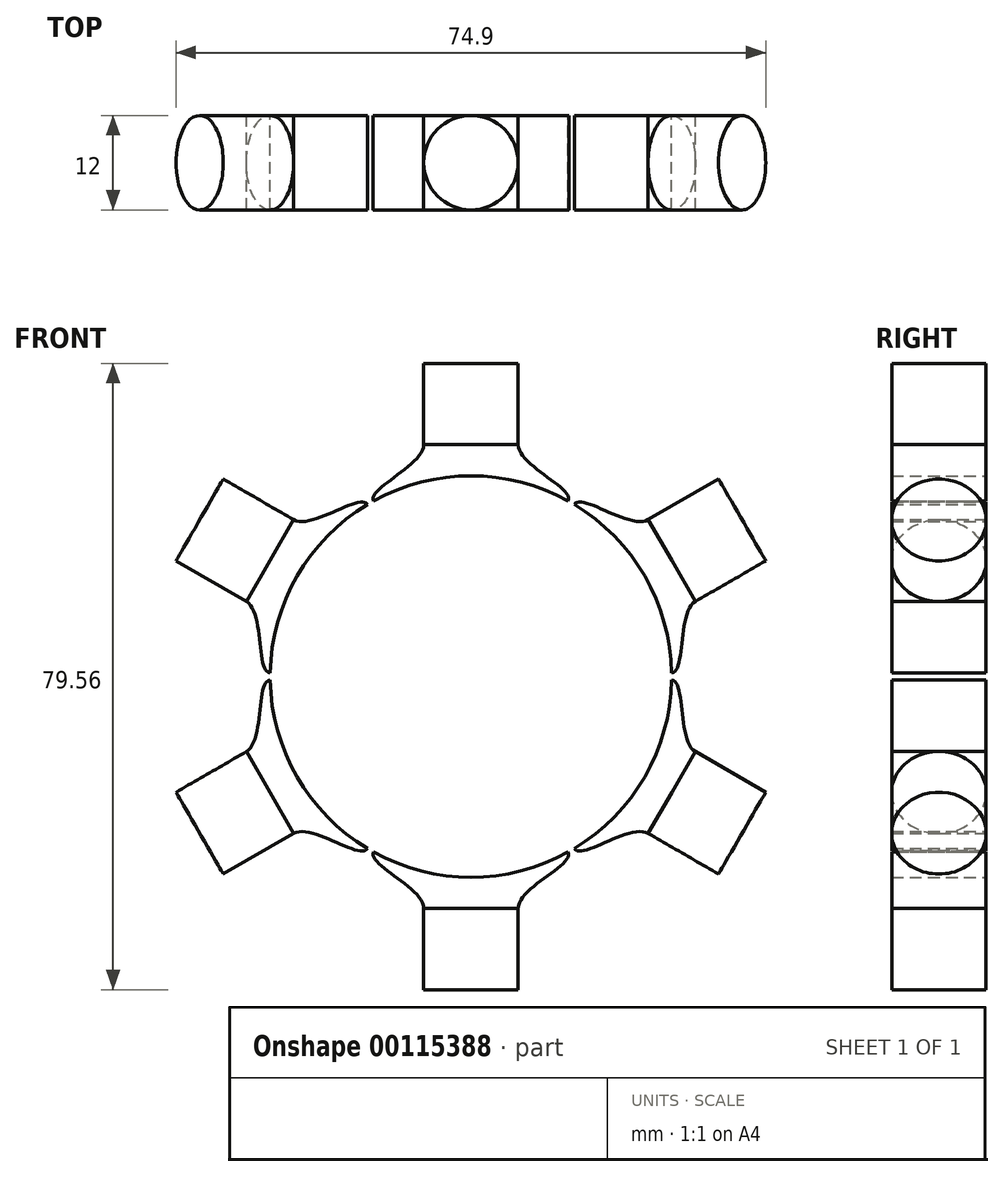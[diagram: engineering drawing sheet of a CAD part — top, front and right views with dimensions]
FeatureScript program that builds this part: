
annotation { "Feature Type Name" : "Feature", "Feature Type Description" : "" }
export const myFeature = defineFeature(function(context is Context, id is Id, definition is map)
    precondition{}
    {
        {
            var Q0;
            Q0=qCreatedBy(makeId("Front.planeOp"),FACE);
            var sketch = newSketch(context, id + "F0", { "sketchPlane" : qUnion([Q0])});
            skCircle(sketch, "E0", {"center": v(0, 0) * mm, "radius": 25.5 * mm});
            skLineSegment(sketch, "E1.top", {"start": v(-6, 39.78) * mm, "end": v(6, 39.78) * mm});
            skLineSegment(sketch, "E1.left", {"start": v(-6, 24.78) * mm, "end": v(-6, 39.78) * mm});
            skLineSegment(sketch, "E1.right", {"start": v(6, 24.78) * mm, "end": v(6, 39.78) * mm});
            skPoint(sketch, "E1.middle", {"position": v(0, 32.28) * mm});
            skFitSpline(sketch, "E2", {"points": [v(-12.35, 22.3) * mm, v(-6, 29.46) * mm], "startDerivative": vector(-2.75, 4.7) * mm, "endDerivative": vector(0, 8.03) * mm});
            skFitSpline(sketch, "E3.MirrorCS", {"points": [v(12.35, 22.3) * mm, v(6, 29.46) * mm], "startDerivative": vector(2.75, 4.7) * mm, "endDerivative": vector(0, 8.03) * mm});
            skLineSegment(sketch, "E4.1.0", {"start": v(-24.46, 7.2) * mm, "end": v(-37.45, 14.7) * mm});
            skLineSegment(sketch, "E4.1.1", {"start": v(-37.45, 14.7) * mm, "end": v(-31.45, 25.09) * mm});
            skLineSegment(sketch, "E4.1.2", {"start": v(-18.46, 17.59) * mm, "end": v(-31.45, 25.09) * mm});
            skLineSegment(sketch, "E4.2.0", {"start": v(-18.46, -17.59) * mm, "end": v(-31.45, -25.09) * mm});
            skLineSegment(sketch, "E4.2.1", {"start": v(-31.45, -25.09) * mm, "end": v(-37.45, -14.7) * mm});
            skLineSegment(sketch, "E4.2.2", {"start": v(-24.46, -7.2) * mm, "end": v(-37.45, -14.7) * mm});
            skLineSegment(sketch, "E4.3.0", {"start": v(6, -24.78) * mm, "end": v(6, -39.78) * mm});
            skLineSegment(sketch, "E4.3.1", {"start": v(6, -39.78) * mm, "end": v(-6, -39.78) * mm});
            skLineSegment(sketch, "E4.3.2", {"start": v(-6, -24.78) * mm, "end": v(-6, -39.78) * mm});
            skLineSegment(sketch, "E4.4.0", {"start": v(24.46, -7.2) * mm, "end": v(37.45, -14.7) * mm});
            skLineSegment(sketch, "E4.4.1", {"start": v(37.45, -14.7) * mm, "end": v(31.45, -25.09) * mm});
            skLineSegment(sketch, "E4.4.2", {"start": v(18.46, -17.59) * mm, "end": v(31.45, -25.09) * mm});
            skLineSegment(sketch, "E4.5.0", {"start": v(18.46, 17.59) * mm, "end": v(31.45, 25.09) * mm});
            skLineSegment(sketch, "E4.5.1", {"start": v(31.45, 25.09) * mm, "end": v(37.45, 14.7) * mm});
            skLineSegment(sketch, "E4.5.2", {"start": v(24.46, 7.2) * mm, "end": v(37.45, 14.7) * mm});
            skFitSpline(sketch, "E5.MirrorCS", {"points": [v(-12.35, -22.3) * mm, v(-6, -29.46) * mm], "startDerivative": vector(-2.75, -4.7) * mm, "endDerivative": vector(0, -8.03) * mm});
            skFitSpline(sketch, "E6.MirrorCS", {"points": [v(12.35, -22.3) * mm, v(6, -29.46) * mm], "startDerivative": vector(2.75, -4.7) * mm, "endDerivative": vector(0, -8.03) * mm});
            skFitSpline(sketch, "E7.MirrorCS", {"points": [v(13.14, 21.85) * mm, v(22.51, 19.93) * mm], "startDerivative": vector(2.7, 4.74) * mm, "endDerivative": vector(6.95, 4.01) * mm});
            skFitSpline(sketch, "E8.MirrorCS", {"points": [v(25.5, 0.46) * mm, v(28.51, 9.53) * mm], "startDerivative": vector(5.45, -0.03) * mm, "endDerivative": vector(6.95, 4.01) * mm});
            skFitSpline(sketch, "E9.MirrorCS", {"points": [v(25.5, -0.46) * mm, v(28.51, -9.53) * mm], "startDerivative": vector(5.45, 0.03) * mm, "endDerivative": vector(6.95, -4.01) * mm});
            skFitSpline(sketch, "E10.MirrorCS", {"points": [v(13.14, -21.85) * mm, v(22.51, -19.93) * mm], "startDerivative": vector(2.7, -4.74) * mm, "endDerivative": vector(6.95, -4.01) * mm});
            skFitSpline(sketch, "E11.MirrorCS", {"points": [v(-25.5, -0.46) * mm, v(-28.51, -9.53) * mm], "startDerivative": vector(-5.45, 0.03) * mm, "endDerivative": vector(-6.95, -4.01) * mm});
            skFitSpline(sketch, "E12.MirrorCS", {"points": [v(-13.14, -21.85) * mm, v(-22.51, -19.93) * mm], "startDerivative": vector(-2.7, -4.74) * mm, "endDerivative": vector(-6.95, -4.01) * mm});
            skFitSpline(sketch, "E13.MirrorCS", {"points": [v(-25.5, 0.46) * mm, v(-28.51, 9.53) * mm], "startDerivative": vector(-5.45, -0.03) * mm, "endDerivative": vector(-6.95, 4.01) * mm});
            skFitSpline(sketch, "E14.MirrorCS", {"points": [v(-13.14, 21.85) * mm, v(-22.51, 19.93) * mm], "startDerivative": vector(-2.7, 4.74) * mm, "endDerivative": vector(-6.95, 4.01) * mm});
            skCircle(sketch, "E15", {"center": v(0, 0) * mm, "radius": 38.5 * mm});
            skCircle(sketch, "E16.0", {"center": v(0, 0) * mm, "radius": 43.5 * mm});
            skLineSegment(sketch, "E17", {"start": v(-6, 29.46) * mm, "end": v(6, 29.46) * mm});
            skLineSegment(sketch, "E18.1.0", {"start": v(-28.51, 9.53) * mm, "end": v(-22.51, 19.93) * mm});
            skLineSegment(sketch, "E18.2.0", {"start": v(-22.51, -19.93) * mm, "end": v(-28.51, -9.53) * mm});
            skLineSegment(sketch, "E19.1.3.0", {"start": v(6, -29.46) * mm, "end": v(-6, -29.46) * mm});
            skLineSegment(sketch, "E19.1.4.0", {"start": v(28.51, -9.53) * mm, "end": v(22.51, -19.93) * mm});
            skLineSegment(sketch, "E19.1.5.0", {"start": v(22.51, 19.93) * mm, "end": v(28.51, 9.53) * mm});
            skSolve(sketch);
        }
        {
            var Q0;
            {var subQ1=sQuery(id+"F0.wireOp",EDGE,"E0");var subQ4=sQuery(id+"F0.wireOp",EDGE,"E1.left");var subQ9=makeQuery(id+"F0.imprint","INTERSECT",VERTEX,{"derivedFrom":[subQ1,subQ4]});Q0=makeQuery(id+"F0.imprint","IMPRINT",FACE,{"disambiguationData":[TD([[makeQuery(id+"F0.imprint","IMPRINT",EDGE,{"disambiguationData":[TD([[subQ9,1.0]])],"derivedFrom":subQ1}),-1.0]])]});}
            var Q1;
            {var subQ3=sQuery(id+"F0.wireOp",EDGE,"E3.MirrorCS");Q1=makeQuery(id+"F0.imprint","IMPRINT",FACE,{"disambiguationData":[TD([[makeQuery(id+"F0.imprint","IMPRINT",EDGE,{"derivedFrom":subQ3}),1.0]])]});}
            var Q2;
            {var subQ3=sQuery(id+"F0.wireOp",EDGE,"E2");Q2=makeQuery(id+"F0.imprint","IMPRINT",FACE,{"disambiguationData":[TD([[makeQuery(id+"F0.imprint","IMPRINT",EDGE,{"derivedFrom":subQ3}),-1.0]])]});}
            var Q3;
            {var subQ3=sQuery(id+"F0.wireOp",EDGE,"E14.MirrorCS");Q3=makeQuery(id+"F0.imprint","IMPRINT",FACE,{"disambiguationData":[TD([[makeQuery(id+"F0.imprint","IMPRINT",EDGE,{"derivedFrom":subQ3}),1.0]])]});}
            var Q4;
            {var subQ1=sQuery(id+"F0.wireOp",EDGE,"E0");var subQ6=sQuery(id+"F0.wireOp",EDGE,"E4.1.0");var subQ9=makeQuery(id+"F0.imprint","INTERSECT",VERTEX,{"derivedFrom":[subQ1,subQ6]});Q4=makeQuery(id+"F0.imprint","IMPRINT",FACE,{"disambiguationData":[TD([[makeQuery(id+"F0.imprint","IMPRINT",EDGE,{"disambiguationData":[TD([[subQ9,1.0]])],"derivedFrom":subQ1}),-1.0]])]});}
            var Q5;
            {var subQ3=sQuery(id+"F0.wireOp",EDGE,"E7.MirrorCS");Q5=makeQuery(id+"F0.imprint","IMPRINT",FACE,{"disambiguationData":[TD([[makeQuery(id+"F0.imprint","IMPRINT",EDGE,{"derivedFrom":subQ3}),-1.0]])]});}
            var Q6;
            {var subQ1=sQuery(id+"F0.wireOp",EDGE,"E0");var subQ4=sQuery(id+"F0.wireOp",EDGE,"E4.5.0");var subQ8=makeQuery(id+"F0.imprint","INTERSECT",VERTEX,{"derivedFrom":[subQ1,subQ4]});Q6=makeQuery(id+"F0.imprint","IMPRINT",FACE,{"disambiguationData":[TD([[makeQuery(id+"F0.imprint","IMPRINT",EDGE,{"disambiguationData":[TD([[subQ8,1.0]])],"derivedFrom":subQ1}),-1.0]])]});}
            var Q7;
            {var subQ3=sQuery(id+"F0.wireOp",EDGE,"E8.MirrorCS");Q7=makeQuery(id+"F0.imprint","IMPRINT",FACE,{"disambiguationData":[TD([[makeQuery(id+"F0.imprint","IMPRINT",EDGE,{"derivedFrom":subQ3}),1.0]])]});}
            var Q8;
            {var subQ3=sQuery(id+"F0.wireOp",EDGE,"E13.MirrorCS");Q8=makeQuery(id+"F0.imprint","IMPRINT",FACE,{"disambiguationData":[TD([[makeQuery(id+"F0.imprint","IMPRINT",EDGE,{"derivedFrom":subQ3}),-1.0]])]});}
            var Q9;
            {var subQ3=sQuery(id+"F0.wireOp",EDGE,"E11.MirrorCS");Q9=makeQuery(id+"F0.imprint","IMPRINT",FACE,{"disambiguationData":[TD([[makeQuery(id+"F0.imprint","IMPRINT",EDGE,{"derivedFrom":subQ3}),1.0]])]});}
            var Q10;
            {var subQ0=sQuery(id+"F0.wireOp",EDGE,"E4.2.0");var subQ4=sQuery(id+"F0.wireOp",EDGE,"E0");var subQ5=makeQuery(id+"F0.imprint","INTERSECT",VERTEX,{"derivedFrom":[subQ4,subQ0]});Q10=makeQuery(id+"F0.imprint","IMPRINT",FACE,{"disambiguationData":[TD([[makeQuery(id+"F0.imprint","IMPRINT",EDGE,{"disambiguationData":[TD([[subQ5,1.0]])],"derivedFrom":subQ4}),-1.0]])]});}
            var Q11;
            {var subQ3=sQuery(id+"F0.wireOp",EDGE,"E12.MirrorCS");Q11=makeQuery(id+"F0.imprint","IMPRINT",FACE,{"disambiguationData":[TD([[makeQuery(id+"F0.imprint","IMPRINT",EDGE,{"derivedFrom":subQ3}),-1.0]])]});}
            var Q12;
            {var subQ3=sQuery(id+"F0.wireOp",EDGE,"E5.MirrorCS");Q12=makeQuery(id+"F0.imprint","IMPRINT",FACE,{"disambiguationData":[TD([[makeQuery(id+"F0.imprint","IMPRINT",EDGE,{"derivedFrom":subQ3}),1.0]])]});}
            var Q13;
            {var subQ1=sQuery(id+"F0.wireOp",EDGE,"E0");var subQ4=sQuery(id+"F0.wireOp",EDGE,"E4.3.0");var subQ5=makeQuery(id+"F0.imprint","INTERSECT",VERTEX,{"derivedFrom":[subQ1,subQ4]});Q13=makeQuery(id+"F0.imprint","IMPRINT",FACE,{"disambiguationData":[TD([[makeQuery(id+"F0.imprint","IMPRINT",EDGE,{"disambiguationData":[TD([[subQ5,1.0]])],"derivedFrom":subQ1}),-1.0]])]});}
            var Q14;
            {var subQ3=sQuery(id+"F0.wireOp",EDGE,"E6.MirrorCS");Q14=makeQuery(id+"F0.imprint","IMPRINT",FACE,{"disambiguationData":[TD([[makeQuery(id+"F0.imprint","IMPRINT",EDGE,{"derivedFrom":subQ3}),-1.0]])]});}
            var Q15;
            {var subQ3=sQuery(id+"F0.wireOp",EDGE,"E10.MirrorCS");Q15=makeQuery(id+"F0.imprint","IMPRINT",FACE,{"disambiguationData":[TD([[makeQuery(id+"F0.imprint","IMPRINT",EDGE,{"derivedFrom":subQ3}),1.0]])]});}
            var Q16;
            {var subQ1=sQuery(id+"F0.wireOp",EDGE,"E0");var subQ4=sQuery(id+"F0.wireOp",EDGE,"E4.4.0");var subQ8=makeQuery(id+"F0.imprint","INTERSECT",VERTEX,{"derivedFrom":[subQ1,subQ4]});Q16=makeQuery(id+"F0.imprint","IMPRINT",FACE,{"disambiguationData":[TD([[makeQuery(id+"F0.imprint","IMPRINT",EDGE,{"disambiguationData":[TD([[subQ8,1.0]])],"derivedFrom":subQ1}),-1.0]])]});}
            var Q17;
            {var subQ3=sQuery(id+"F0.wireOp",EDGE,"E9.MirrorCS");Q17=makeQuery(id+"F0.imprint","IMPRINT",FACE,{"disambiguationData":[TD([[makeQuery(id+"F0.imprint","IMPRINT",EDGE,{"derivedFrom":subQ3}),-1.0]])]});}
            extrude(context, id + "F1", {"entities" : qUnion([Q0, Q1, Q2, Q3, Q4, Q5, Q6, Q7, Q8, Q9, Q10, Q11, Q12, Q13, Q14, Q15, Q16, Q17]), "endBound" : BoundingType.SYMMETRIC, "depth" : 12 * mm});
        }
        {
            var Q0;
            Q0=makeQuery(id+"F1.opExtrude","SWEPT_FACE",FACE,{"disambiguationData":[OSD([sQuery(id+"F0.wireOp",EDGE,"E17")])]});
            var sketch = newSketch(context, id + "F2", { "sketchPlane" : qUnion([Q0])});
            skCircle(sketch, "E20", {"center": v(0, 0) * mm, "radius": 6 * mm});
            skSolve(sketch);
        }
        {
            var Q0;
            {var subQ0=sQuery(id+"F2.wireOp",EDGE,"E20");var subQ1=sQuery(id+"F0.wireOp",EDGE,"E17");var subQ2=makeQuery(id+"F2.imprint","INTERSECT",VERTEX,{"derivedFrom":[makeQuery(id+"F1.opExtrude","CAP_EDGE",EDGE,{"disambiguationData":[OSD([subQ1])],"isStart":true}),subQ0]});Q0=makeQuery(id+"F2.imprint","IMPRINT",FACE,{"disambiguationData":[TD([[makeQuery(id+"F2.imprint","IMPRINT",EDGE,{"disambiguationData":[TD([[subQ2,1.0]])],"derivedFrom":subQ0}),1.0]])]});}
            extrude(context, id + "F3", {"entities" : qUnion([Q0]), "operationType" : NewBodyOperationType.ADD, "depth" : 10.32 * mm});
        }
        {
            var Q0;
            Q0=makeQuery(id+"F1.opExtrude","SWEPT_BODY",BODY,{"disambiguationData":[OSD([sQuery(id+"F0.wireOp",EDGE,"E0"),sQuery(id+"F0.wireOp",EDGE,"E2"),sQuery(id+"F0.wireOp",EDGE,"E3.MirrorCS"),sQuery(id+"F0.wireOp",EDGE,"E17")])]});
            var Q1;
            Q1=qCreatedBy(makeId("Top.planeOp"),FACE);
            mirror(context, id + "F4", {"operationType" : NewBodyOperationType.ADD, "entities" : qUnion([Q0]), "mirrorPlane" : qUnion([Q1])});
        }
        {
            var Q0;
            Q0=makeQuery(id+"F1.opExtrude","SWEPT_FACE",FACE,{"disambiguationData":[OSD([sQuery(id+"F0.wireOp",EDGE,"E19.1.5.0")])]});
            var sketch = newSketch(context, id + "F5", { "sketchPlane" : qUnion([Q0])});
            skCircle(sketch, "E21", {"center": v(0, 0) * mm, "radius": 6 * mm});
            skSolve(sketch);
        }
        {
            var Q0;
            {var subQ0=sQuery(id+"F5.wireOp",EDGE,"E21");var subQ1=sQuery(id+"F0.wireOp",EDGE,"E19.1.5.0");var subQ3=makeQuery(id+"F5.imprint","INTERSECT",VERTEX,{"derivedFrom":[makeQuery(id+"F1.opExtrude","CAP_EDGE",EDGE,{"disambiguationData":[OSD([subQ1])],"isStart":true}),subQ0]});Q0=makeQuery(id+"F5.imprint","IMPRINT",FACE,{"disambiguationData":[TD([[makeQuery(id+"F5.imprint","IMPRINT",EDGE,{"disambiguationData":[TD([[subQ3,-1.0]])],"derivedFrom":subQ0}),1.0]])]});}
            extrude(context, id + "F6", {"entities" : qUnion([Q0]), "operationType" : NewBodyOperationType.ADD, "depth" : 10.32 * mm});
        }
        {
            var Q0;
            Q0=makeQuery(id+"F1.opExtrude","SWEPT_FACE",FACE,{"disambiguationData":[OSD([sQuery(id+"F0.wireOp",EDGE,"E19.1.4.0")])]});
            var sketch = newSketch(context, id + "F7", { "sketchPlane" : qUnion([Q0])});
            skCircle(sketch, "E22", {"center": v(0, 0) * mm, "radius": 6 * mm});
            skSolve(sketch);
        }
        {
            var Q0;
            {var subQ0=sQuery(id+"F7.wireOp",EDGE,"E22");var subQ1=sQuery(id+"F0.wireOp",EDGE,"E19.1.4.0");var subQ3=makeQuery(id+"F7.imprint","INTERSECT",VERTEX,{"derivedFrom":[makeQuery(id+"F1.opExtrude","CAP_EDGE",EDGE,{"disambiguationData":[OSD([subQ1])],"isStart":true}),subQ0]});Q0=makeQuery(id+"F7.imprint","IMPRINT",FACE,{"disambiguationData":[TD([[makeQuery(id+"F7.imprint","IMPRINT",EDGE,{"disambiguationData":[TD([[subQ3,-1.0]])],"derivedFrom":subQ0}),1.0]])]});}
            extrude(context, id + "F8", {"entities" : qUnion([Q0]), "operationType" : NewBodyOperationType.ADD, "depth" : 10.32 * mm});
        }
        {
            var Q0;
            Q0=makeQuery(id+"F1.opExtrude","SWEPT_FACE",FACE,{"disambiguationData":[OSD([sQuery(id+"F0.wireOp",EDGE,"E18.1.0")])]});
            var sketch = newSketch(context, id + "F9", { "sketchPlane" : qUnion([Q0])});
            skCircle(sketch, "E23", {"center": v(0, 0) * mm, "radius": 6 * mm});
            skSolve(sketch);
        }
        {
            var Q0;
            Q0 = qSketchRegion(id + "F9", true);
            var Q1;
            {var subQ0=sQuery(id+"F9.wireOp",EDGE,"E23");var subQ1=sQuery(id+"F0.wireOp",EDGE,"E18.1.0");var subQ3=makeQuery(id+"F9.imprint","INTERSECT",VERTEX,{"derivedFrom":[makeQuery(id+"F1.opExtrude","CAP_EDGE",EDGE,{"disambiguationData":[OSD([subQ1])],"isStart":false}),subQ0]});Q1=makeQuery(id+"F9.imprint","IMPRINT",FACE,{"disambiguationData":[TD([[makeQuery(id+"F9.imprint","IMPRINT",EDGE,{"disambiguationData":[TD([[subQ3,-1.0]])],"derivedFrom":subQ0}),1.0]])]});}
            extrude(context, id + "F10", {"entities" : qUnion([Q0, Q1]), "operationType" : NewBodyOperationType.ADD, "depth" : 10.32 * mm});
        }
        {
            var Q0;
            Q0=makeQuery(id+"F1.opExtrude","SWEPT_FACE",FACE,{"disambiguationData":[OSD([sQuery(id+"F0.wireOp",EDGE,"E18.2.0")])]});
            var sketch = newSketch(context, id + "F11", { "sketchPlane" : qUnion([Q0])});
            skCircle(sketch, "E24", {"center": v(0, 0) * mm, "radius": 6 * mm});
            skSolve(sketch);
        }
        {
            var Q0;
            Q0 = qSketchRegion(id + "F11", true);
            var Q1;
            {var subQ0=sQuery(id+"F11.wireOp",EDGE,"E24");var subQ1=sQuery(id+"F0.wireOp",EDGE,"E18.2.0");var subQ3=makeQuery(id+"F11.imprint","INTERSECT",VERTEX,{"derivedFrom":[makeQuery(id+"F1.opExtrude","CAP_EDGE",EDGE,{"disambiguationData":[OSD([subQ1])],"isStart":false}),subQ0]});Q1=makeQuery(id+"F11.imprint","IMPRINT",FACE,{"disambiguationData":[TD([[makeQuery(id+"F11.imprint","IMPRINT",EDGE,{"disambiguationData":[TD([[subQ3,-1.0]])],"derivedFrom":subQ0}),1.0]])]});}
            extrude(context, id + "F12", {"entities" : qUnion([Q0, Q1]), "operationType" : NewBodyOperationType.ADD, "depth" : 10.32 * mm});
        }
    });
